# Revit family: Coat Hook_Metlam_Collapsible_Concealed Fix
name_source: partatom
category: Specialty Equipment
revit_build: Autodesk Revit 2016 (Build: 20190508_0715(x64)
units: mm (PartAtom-declared; Revit-internal decimal feet)

## family parameters
Always vertical = Yes
Cut with Voids When Loaded = No
OmniClass Number = 23.40.20.21.31
Part Type = Normal
Room Calculation Point = Yes
Round Connector Dimension = Use Diameter
Shared = No
Work Plane-Based = No

## types (1)
- 108w x 56d x 108h (ML2122)
    Description = Concealed Fix Collapsible Coat Hook
    Manufacturer = Metlam
    Manufacturer_Overall Depth = 56 mm  [stored 0.183727 ft]
    Manufacturer_Overall Height = 108 mm  [stored 0.354331 ft]
    Manufacturer_Overall Width = 108 mm  [stored 0.354331 ft]
    Manufacturer_Spec Code = ML2122
    Manufacturer_URL__Product Specific = https://metlam.com.au
    Material_ANZRS = z_Metlam_Metal_Stainless Steel_Satin
    Model = ML2122
    Type Comments = Coat Hooks
    URL = http://www.metlam.com.au

note: [stored X ft] marks values corroborated as IEEE doubles in the binary element streams (Revit-internal decimal feet)

## geometry (parser evidence)
native form markers: Sweep x3
no freeform markers — native parametric forms only
